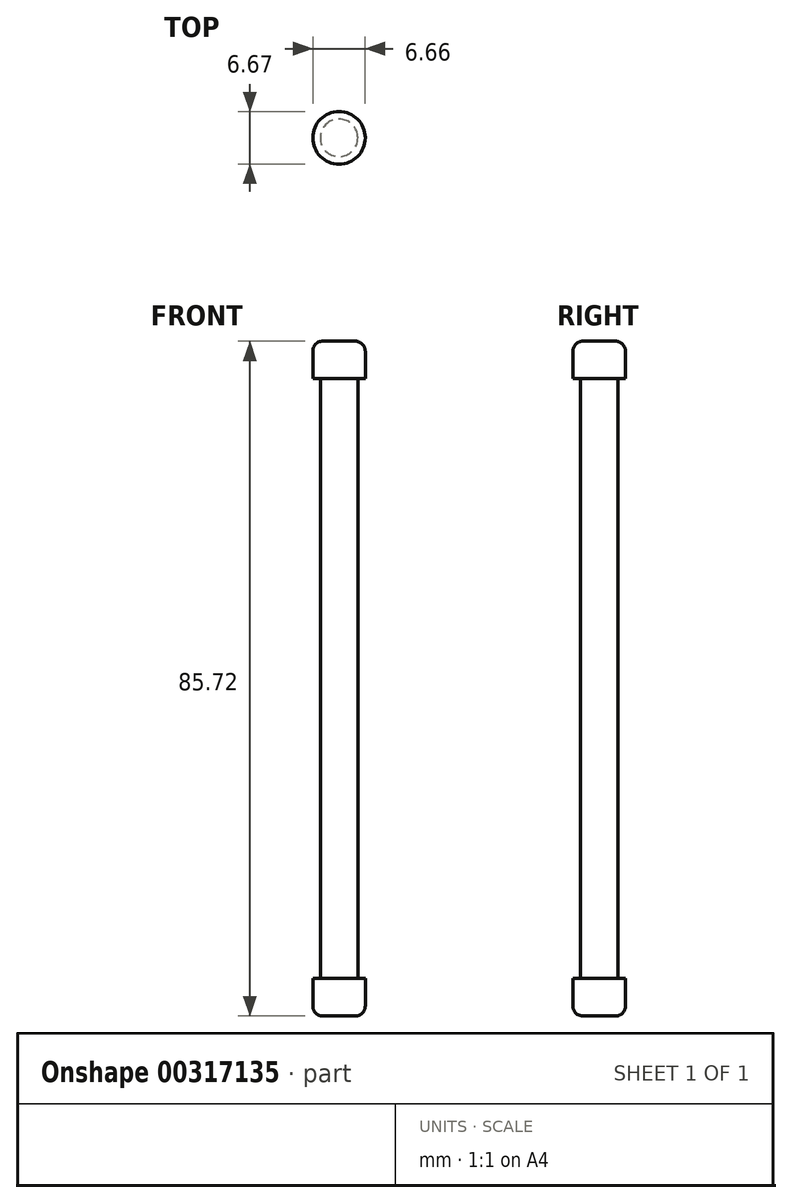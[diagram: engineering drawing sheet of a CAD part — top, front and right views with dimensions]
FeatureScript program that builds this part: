
annotation { "Feature Type Name" : "Feature", "Feature Type Description" : "" }
export const myFeature = defineFeature(function(context is Context, id is Id, definition is map)
    precondition{}
    {
        {
            var Q0;
            Q0=qCreatedBy(makeId("Top.planeOp"),FACE);
            var sketch = newSketch(context, id + "F0", { "sketchPlane" : qUnion([Q0])});
            skCircle(sketch, "E0", {"center": v(-29.11, -9.7) * mm, "radius": 2.38 * mm});
            skSolve(sketch);
        }
        {
            var Q0;
            Q0=qSketchRegion(id+"F0",true);
            extrude(context, id + "F1", {"entities" : qUnion([Q0]), "depth" : 76.2 * mm});
        }
        {
            var Q0;
            Q0=makeQuery(id+"F1.opExtrude","CAP_FACE",FACE,{"disambiguationData":[OSD([sQuery(id+"F0.wireOp",EDGE,"E0")])],"isStart":false});
            var sketch = newSketch(context, id + "F2", { "sketchPlane" : qUnion([Q0])});
            skCircle(sketch, "E1", {"center": v(-29.11, -9.7) * mm, "radius": 3.33 * mm});
            skSolve(sketch);
        }
        {
            var Q0;
            Q0=qSketchRegion(id+"F2",true);
            extrude(context, id + "F3", {"entities" : qUnion([Q0]), "operationType" : NewBodyOperationType.ADD, "depth" : 4.76 * mm});
        }
        {
            var Q0;
            Q0=makeQuery(id+"F1.opExtrude","CAP_FACE",FACE,{"disambiguationData":[OSD([sQuery(id+"F0.wireOp",EDGE,"E0")])],"isStart":true});
            var sketch = newSketch(context, id + "F4", { "sketchPlane" : qUnion([Q0])});
            skCircle(sketch, "E2", {"center": v(-29.11, 9.7) * mm, "radius": 3.33 * mm});
            skSolve(sketch);
        }
        {
            var Q0;
            Q0=qSketchRegion(id+"F4",true);
            extrude(context, id + "F5", {"entities" : qUnion([Q0]), "operationType" : NewBodyOperationType.ADD, "depth" : 4.76 * mm});
        }
        {
            var Q0;
            Q0=makeQuery(id+"F5.opExtrude","CAP_EDGE",EDGE,{"disambiguationData":[OSD([sQuery(id+"F4.wireOp",EDGE,"E2")])],"isStart":false});
            fillet(context, id + "F6", {"entities" : qUnion([Q0]), "radius" : 1.27 * mm, "tangentPropagation" : true, "allowEdgeOverflow" : false});
        }
        {
            var Q0;
            Q0=makeQuery(id+"F3.opExtrude","CAP_EDGE",EDGE,{"disambiguationData":[OSD([sQuery(id+"F2.wireOp",EDGE,"E1")])],"isStart":false});
            fillet(context, id + "F7", {"entities" : qUnion([Q0]), "radius" : 1.27 * mm, "tangentPropagation" : true, "allowEdgeOverflow" : false});
        }
    });
